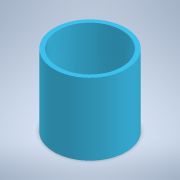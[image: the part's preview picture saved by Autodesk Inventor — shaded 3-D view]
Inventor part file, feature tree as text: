
AUTODESK INVENTOR PART (.ipt)
format: ipt  version: 2020 (Build 240168000, 168)  size: 108,544 bytes
history: native  units: mm
features: other x1, extrude x1, sketch x1
ambient origin geometry x8: Origin, YZ Plane, XZ Plane, XY Plane, X Axis, Y Axis, Z Axis, Center Point
bodies: Body1 (feature_tree)
feature tree (3):
  other  "Твердое тело1"
  extrude  "Выдавливание1"  Depth=50.0mm
  sketch  "Эскиз1"
